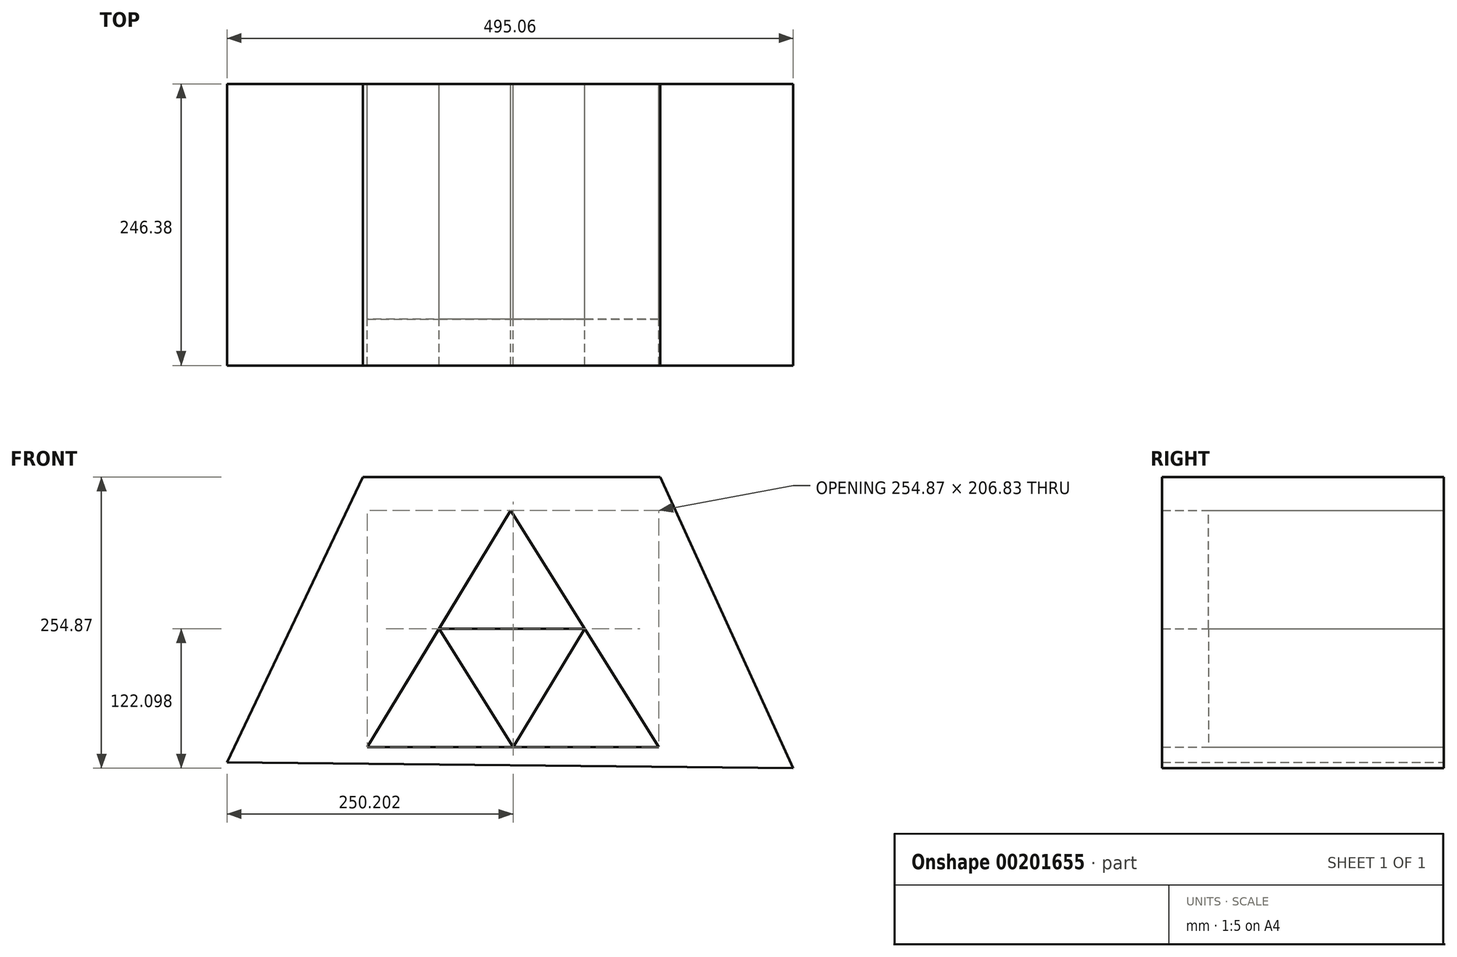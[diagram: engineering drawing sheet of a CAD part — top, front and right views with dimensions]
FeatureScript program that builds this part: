
annotation { "Feature Type Name" : "Feature", "Feature Type Description" : "" }
export const myFeature = defineFeature(function(context is Context, id is Id, definition is map)
    precondition{}
    {
        {
            var Q0;
            Q0=qCreatedBy(makeId("Front.planeOp"),FACE);
            var sketch = newSketch(context, id + "F0", { "sketchPlane" : qUnion([Q0])});
            skLineSegment(sketch, "E0", {"start": v(-1393.14, -779.94) * mm, "end": v(-1274.38, -530.4) * mm});
            skLineSegment(sketch, "E1", {"start": v(-1274.38, -530.4) * mm, "end": v(-1014.17, -530.4) * mm});
            skLineSegment(sketch, "E2", {"start": v(-1014.17, -530.4) * mm, "end": v(-898.08, -785.28) * mm});
            skLineSegment(sketch, "E3", {"start": v(-898.08, -785.28) * mm, "end": v(-1393.14, -779.94) * mm});
            skLineSegment(sketch, "E4", {"start": v(-1270.37, -766.6) * mm, "end": v(-1144.94, -559.77) * mm});
            skLineSegment(sketch, "E5", {"start": v(-1144.94, -559.77) * mm, "end": v(-1015.5, -766.6) * mm});
            skLineSegment(sketch, "E6", {"start": v(-1015.5, -766.6) * mm, "end": v(-1270.37, -766.6) * mm});
            skLineSegment(sketch, "E7", {"start": v(-1207.66, -663.18) * mm, "end": v(-1142.94, -766.6) * mm});
            skLineSegment(sketch, "E8", {"start": v(-1142.94, -766.6) * mm, "end": v(-1080.22, -663.18) * mm});
            skLineSegment(sketch, "E9", {"start": v(-1080.22, -663.18) * mm, "end": v(-1207.66, -663.18) * mm});
            skLineSegment(sketch, "E10", {"start": v(-1163.63, -505.26) * mm, "end": v(-1163.63, 145.2) * mm});
            skLineSegment(sketch, "E11", {"start": v(-1124, 145.2) * mm, "end": v(-1124, -505.26) * mm});
            skLineSegment(sketch, "E12", {"start": v(-1124, 145.2) * mm, "end": v(-1089.46, 163.58) * mm});
            skLineSegment(sketch, "E13", {"start": v(-1089.46, 163.58) * mm, "end": v(-1089.46, 200.33) * mm});
            skLineSegment(sketch, "E14", {"start": v(-1089.46, 200.33) * mm, "end": v(-1113.5, 225.78) * mm});
            skLineSegment(sketch, "E15", {"start": v(-1113.5, 225.78) * mm, "end": v(-1113.5, 271.02) * mm});
            skLineSegment(sketch, "E16", {"start": v(-1113.5, 271.02) * mm, "end": v(-1113.5, 273.91) * mm});
            skLineSegment(sketch, "E17", {"start": v(-1113.5, 273.91) * mm, "end": v(-1103.9, 273.91) * mm});
            skLineSegment(sketch, "E18", {"start": v(-1103.9, 273.91) * mm, "end": v(-1103.9, 291.99) * mm});
            skLineSegment(sketch, "E19", {"start": v(-1103.9, 291.99) * mm, "end": v(-1108.1, 294.09) * mm});
            skLineSegment(sketch, "E20", {"start": v(-1108.1, 294.09) * mm, "end": v(-1108.1, 326.24) * mm});
            skLineSegment(sketch, "E21", {"start": v(-1108.1, 326.24) * mm, "end": v(-1072.34, 352.36) * mm});
            skFitSpline(sketch, "E22", {"points": [v(-1072.34, 352.36) * mm, v(-1065.66, 344.35) * mm, v(-1060.99, 330.54) * mm], "startDerivative": vector(15.94, -15.66) * mm, "endDerivative": vector(7.02, -27.65) * mm});
            skLineSegment(sketch, "E23", {"start": v(-1060.99, 330.54) * mm, "end": v(-981.06, 310.73) * mm});
            skFitSpline(sketch, "E24", {"points": [v(-981.06, 310.73) * mm, v(-983.06, 320.97) * mm, v(-999.54, 352.36) * mm, v(-1026.03, 385.76) * mm, v(-1053.66, 401.77) * mm], "startDerivative": vector(-5.7, 58.66) * mm, "endDerivative": vector(-87.07, 64.12) * mm});
            skFitSpline(sketch, "E25", {"points": [v(-1053.66, 401.77) * mm, v(-1053.66, 430.3) * mm], "startDerivative": vector(0, 24.5) * mm, "endDerivative": vector(0, 24.5) * mm});
            skFitSpline(sketch, "E26", {"points": [v(-1053.66, 430.3) * mm, v(-1054.98, 427.4) * mm, v(-1067.44, 408.47) * mm, v(-1095.28, 392) * mm], "startDerivative": vector(-33.5, -6.03) * mm, "endDerivative": vector(-72.93, -30.35) * mm});
            skLineSegment(sketch, "E27", {"start": v(-1095.28, 392) * mm, "end": v(-1098.17, 392) * mm});
            skFitSpline(sketch, "E28", {"points": [v(-1098.17, 392) * mm, v(-1095.28, 394.9) * mm, v(-1091.5, 405.13) * mm, v(-1095.28, 418.5) * mm, v(-1117.64, 429.85) * mm], "startDerivative": vector(19.84, 15.78) * mm, "endDerivative": vector(-73.55, 26.6) * mm});
            skLineSegment(sketch, "E29", {"start": v(-1117.64, 429.85) * mm, "end": v(-1117.64, 438.04) * mm});
            skLineSegment(sketch, "E30", {"start": v(-1117.64, 438.04) * mm, "end": v(-1124, 440.98) * mm});
            skLineSegment(sketch, "E31", {"start": v(-1124, 440.98) * mm, "end": v(-1124, 679.27) * mm});
            skLineSegment(sketch, "E32", {"start": v(-1124, 679.27) * mm, "end": v(-1117.64, 679.27) * mm});
            skLineSegment(sketch, "E33", {"start": v(-1117.64, 679.27) * mm, "end": v(-1117.64, 689.47) * mm});
            skLineSegment(sketch, "E34", {"start": v(-1117.64, 689.47) * mm, "end": v(-1104.95, 711.37) * mm});
            skLineSegment(sketch, "E35", {"start": v(-1104.95, 711.37) * mm, "end": v(-1127.8, 755.19) * mm});
            skLineSegment(sketch, "E36", {"start": v(-1127.8, 755.19) * mm, "end": v(-1140.15, 758.18) * mm});
            skLineSegment(sketch, "E37", {"start": v(-1140.15, 758.18) * mm, "end": v(-1150.26, 758.18) * mm});
            skLineSegment(sketch, "E38", {"start": v(-1150.26, 758.18) * mm, "end": v(-1178.72, 715.87) * mm});
            skLineSegment(sketch, "E39", {"start": v(-1178.72, 715.87) * mm, "end": v(-1168.98, 690.4) * mm});
            skLineSegment(sketch, "E40", {"start": v(-1168.98, 690.4) * mm, "end": v(-1168.98, 683.67) * mm});
            skLineSegment(sketch, "E41", {"start": v(-1168.98, 683.67) * mm, "end": v(-1164.52, 679.27) * mm});
            skLineSegment(sketch, "E42", {"start": v(-1164.52, 679.27) * mm, "end": v(-1164.52, 438.04) * mm});
            skLineSegment(sketch, "E43", {"start": v(-1166.83, 200.3) * mm, "end": v(-1146.6, 161.37) * mm});
            skLineSegment(sketch, "E44", {"start": v(-1146.6, 161.37) * mm, "end": v(-1122.27, 198.81) * mm});
            skLineSegment(sketch, "E45", {"start": v(-1122.27, 198.81) * mm, "end": v(-1166.83, 200.3) * mm});
            skLineSegment(sketch, "E46", {"start": v(-1156.72, 180.84) * mm, "end": v(-1144.55, 199.56) * mm});
            skLineSegment(sketch, "E47", {"start": v(-1144.55, 199.56) * mm, "end": v(-1134.44, 180.09) * mm});
            skLineSegment(sketch, "E48", {"start": v(-1134.44, 180.09) * mm, "end": v(-1156.72, 180.84) * mm});
            skLineSegment(sketch, "E49.MirrorCS", {"start": v(-1176.63, 229.03) * mm, "end": v(-1176.46, 274.27) * mm});
            skLineSegment(sketch, "E50.MirrorCS", {"start": v(-1185.74, 274.05) * mm, "end": v(-1185.67, 292.12) * mm});
            skLineSegment(sketch, "E51.MirrorCS", {"start": v(-1176.45, 274.02) * mm, "end": v(-1186.05, 274.05) * mm});
            skLineSegment(sketch, "E52.MirrorCS", {"start": v(-1179.9, 294.23) * mm, "end": v(-1185.67, 292.12) * mm});
            skLineSegment(sketch, "E53.MirrorCS", {"start": v(-1179.9, 294.23) * mm, "end": v(-1179.77, 327.25) * mm});
            skLineSegment(sketch, "E54.MirrorCS", {"start": v(-1229.55, 328.94) * mm, "end": v(-1300.88, 311.31) * mm});
            skFitSpline(sketch, "E55.MirrorCS", {"points": [v(-1300.88, 311.31) * mm, v(-1298.84, 321.55) * mm, v(-1282.25, 352.88) * mm, v(-1255.63, 386.18) * mm, v(-1236.32, 403) * mm], "startDerivative": vector(5.92, 58.64) * mm, "endDerivative": vector(87.3, 63.8) * mm});
            skFitSpline(sketch, "E56", {"points": [v(-1229.55, 328.94) * mm, v(-1225.46, 339.33) * mm, v(-1217.59, 352.56) * mm], "startDerivative": vector(7.6, 22.15) * mm, "endDerivative": vector(16.11, 25) * mm});
            skFitSpline(sketch, "E57", {"points": [v(-1217.59, 352.56) * mm, v(-1202.47, 338.39) * mm, v(-1182.64, 327.68) * mm, v(-1184.52, 328.94) * mm], "startDerivative": vector(27.33, -32.72) * mm, "endDerivative": vector(-21.7, 13.17) * mm});
            skLineSegment(sketch, "E58", {"start": v(-1182.64, 327.68) * mm, "end": v(-1179.77, 327.25) * mm});
            skLineSegment(sketch, "E59", {"start": v(-1163.63, 145.2) * mm, "end": v(-1195.7, 164.67) * mm});
            skLineSegment(sketch, "E60", {"start": v(-1195.7, 164.67) * mm, "end": v(-1195.7, 201.47) * mm});
            skLineSegment(sketch, "E61", {"start": v(-1195.7, 201.47) * mm, "end": v(-1176.63, 229.03) * mm});
            skLineSegment(sketch, "E62", {"start": v(-1163.63, -505.26) * mm, "end": v(-1124, -505.26) * mm});
            skLineSegment(sketch, "E63.MirrorCS", {"start": v(-1173.2, 436.2) * mm, "end": v(-1164.52, 438.04) * mm});
            skLineSegment(sketch, "E64.MirrorCS", {"start": v(-1172.7, 430.43) * mm, "end": v(-1173.2, 436.2) * mm});
            skFitSpline(sketch, "E65.MirrorCS", {"points": [v(-1191.95, 392.63) * mm, v(-1194.8, 395.56) * mm, v(-1198.45, 405.85) * mm, v(-1194.49, 419.16) * mm, v(-1172.52, 430.22) * mm], "startDerivative": vector(-19.63, 16.05) * mm, "endDerivative": vector(73.9, 25.61) * mm});
            skFitSpline(sketch, "E66.MirrorCS", {"points": [v(-1235.94, 431.51) * mm, v(-1234.66, 428.6) * mm, v(-1222.45, 409.51) * mm, v(-1194.84, 392.66) * mm], "startDerivative": vector(33.42, -6.48) * mm, "endDerivative": vector(72.52, -31.33) * mm});
            skLineSegment(sketch, "E67.MirrorCS", {"start": v(-1194.84, 392.66) * mm, "end": v(-1191.95, 392.63) * mm});
            skFitSpline(sketch, "E68.MirrorCS", {"points": [v(-1236.32, 403) * mm, v(-1235.94, 431.51) * mm], "startDerivative": vector(0.33, 24.49) * mm, "endDerivative": vector(0.33, 24.49) * mm});
            skFitSpline(sketch, "E69.MirrorCS", {"points": [v(-1300.88, 311.31) * mm, v(-1298.84, 321.55) * mm, v(-1282.25, 352.88) * mm, v(-1255.63, 386.18) * mm, v(-1236.32, 403) * mm], "startDerivative": vector(5.92, 58.64) * mm, "endDerivative": vector(87.3, 63.8) * mm});
            skSolve(sketch);
        }
        {
            var Q0;
            Q0=makeQuery(id+"F0.imprint","IMPRINT",FACE,{"disambiguationData":[TD([[makeQuery(id+"F0.imprint","IMPRINT",EDGE,{"derivedFrom":sQuery(id+"F0.wireOp",EDGE,"E0")}),-1.0]])]});
            var Q1;
            Q1=makeQuery(id+"F0.imprint","IMPRINT",FACE,{"disambiguationData":[TD([[makeQuery(id+"F0.imprint","IMPRINT",EDGE,{"derivedFrom":sQuery(id+"F0.wireOp",EDGE,"E7")}),1.0]])]});
            extrude(context, id + "F1", {"entities" : qUnion([Q0, Q1]), "depth" : 246.38 * mm});
        }
        {
            var Q0;
            {var subQ3=sQuery(id+"F0.wireOp",EDGE,"E9");Q0=makeQuery(id+"F0.imprint","IMPRINT",FACE,{"disambiguationData":[TD([[makeQuery(id+"F0.imprint","IMPRINT",EDGE,{"derivedFrom":subQ3}),-1.0]])]});}
            var Q1;
            {var subQ3=sQuery(id+"F0.wireOp",EDGE,"E8");Q1=makeQuery(id+"F0.imprint","IMPRINT",FACE,{"disambiguationData":[TD([[makeQuery(id+"F0.imprint","IMPRINT",EDGE,{"derivedFrom":subQ3}),-1.0]])]});}
            var Q2;
            {var subQ3=sQuery(id+"F0.wireOp",EDGE,"E7");Q2=makeQuery(id+"F0.imprint","IMPRINT",FACE,{"disambiguationData":[TD([[makeQuery(id+"F0.imprint","IMPRINT",EDGE,{"derivedFrom":subQ3}),-1.0]])]});}
            extrude(context, id + "F2", {"entities" : qUnion([Q0, Q1, Q2]), "depth" : 205.74 * mm});
        }
    });
